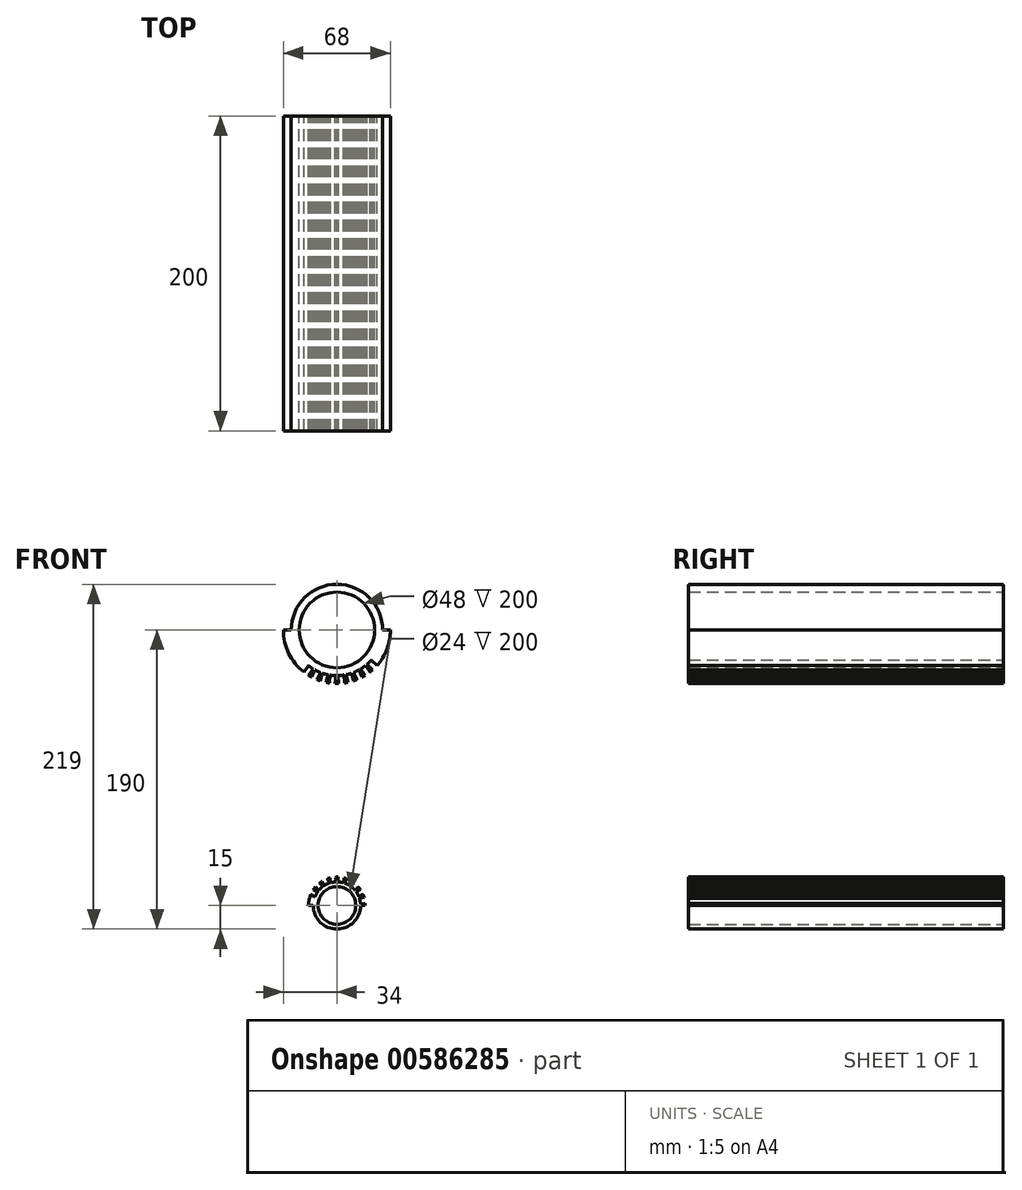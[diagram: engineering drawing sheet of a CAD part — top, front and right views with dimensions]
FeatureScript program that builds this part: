
annotation { "Feature Type Name" : "Feature", "Feature Type Description" : "" }
export const myFeature = defineFeature(function(context is Context, id is Id, definition is map)
    precondition{}
    {
        {
            var Q0;
            Q0=qCreatedBy(makeId("Front.planeOp"),FACE);
            cPlane(context, id + "F0", {"entities" : qUnion([Q0]), "cplaneType" : CPlaneType.OFFSET, "offset" : 100 * mm, "oppositeDirection" : true, "width" : 150 * mm, "height" : 150 * mm});
        }
        {
            var Q0;
            Q0=qCreatedBy(id+"F0.planeOp",FACE);
            var sketch = newSketch(context, id + "F1", { "sketchPlane" : qUnion([Q0])});
            skCircle(sketch, "E0", {"center": v(0, 0) * mm, "radius": 24 * mm});
            skArc(sketch, "E1", {"start": v(-18.13, -22.63) * mm, "mid": v(2.53, -28.89) * mm, "end": v(21.79, -19.14) * mm});
            skArc(sketch, "E2", {"start": v(-34, 0) * mm, "mid": v(-30.58, -14.86) * mm, "end": v(-21, -26.73) * mm});
            skLineSegment(sketch, "E3", {"start": v(-34, 0) * mm, "end": v(-29, 0) * mm});
            skLineSegment(sketch, "E4", {"start": v(29, 0) * mm, "end": v(34, 0) * mm});
            skLineSegment(sketch, "E5", {"start": v(-54.4, 0) * mm, "end": v(73.62, 0) * mm, "construction": true});
            skPoint(sketch, "E5.startSnap0", {"position": v(-31.5, 0) * mm});
            skLineSegment(sketch, "E6", {"start": v(0, 47.74) * mm, "end": v(0, -182.93) * mm, "construction": true});
            skLineSegment(sketch, "E7", {"start": v(0, 0) * mm, "end": v(2.1, -23.9) * mm, "construction": true});
            skLineSegment(sketch, "E8", {"start": v(2.1, -23.9) * mm, "end": v(2.53, -28.89) * mm, "construction": true});
            skLineSegment(sketch, "E9", {"start": v(2.53, -28.89) * mm, "end": v(3.01, -34.45) * mm});
            skLineSegment(sketch, "E10", {"start": v(4.83, -33.66) * mm, "end": v(4.4, -28.67) * mm});
            skLineSegment(sketch, "E11", {"start": v(1.1, -33.98) * mm, "end": v(0.65, -29) * mm});
            skLineSegment(sketch, "E12", {"start": v(0, 0) * mm, "end": v(6.21, -23.18) * mm, "construction": true});
            skLineSegment(sketch, "E13", {"start": v(7.5, -28.01) * mm, "end": v(8.74, -32.61) * mm});
            skLineSegment(sketch, "E14", {"start": v(6.21, -23.18) * mm, "end": v(7.5, -28.01) * mm, "construction": true});
            skLineSegment(sketch, "E15", {"start": v(5.68, -28.44) * mm, "end": v(6.98, -33.28) * mm});
            skLineSegment(sketch, "E16", {"start": v(9.3, -27.47) * mm, "end": v(10.6, -32.3) * mm});
            skLineSegment(sketch, "E17", {"start": v(0, 0) * mm, "end": v(10.14, -21.75) * mm, "construction": true});
            skLineSegment(sketch, "E18", {"start": v(12.65, -31.56) * mm, "end": v(10.53, -27.02) * mm});
            skLineSegment(sketch, "E19", {"start": v(13.93, -25.44) * mm, "end": v(16.05, -29.98) * mm});
            skLineSegment(sketch, "E20", {"start": v(12.26, -26.28) * mm, "end": v(14.23, -30.51) * mm});
            skLineSegment(sketch, "E21", {"start": v(10.14, -21.75) * mm, "end": v(12.26, -26.28) * mm, "construction": true});
            skLineSegment(sketch, "E22", {"start": v(0, 0) * mm, "end": v(13.77, -19.66) * mm, "construction": true});
            skLineSegment(sketch, "E23", {"start": v(18.13, -22.63) * mm, "end": v(21, -26.73) * mm});
            skLineSegment(sketch, "E24", {"start": v(15.06, -24.78) * mm, "end": v(17.94, -28.88) * mm});
            skLineSegment(sketch, "E25", {"start": v(16.63, -23.76) * mm, "end": v(19.52, -27.88) * mm});
            skLineSegment(sketch, "E26", {"start": v(13.77, -19.66) * mm, "end": v(16.63, -23.76) * mm, "construction": true});
            skLineSegment(sketch, "E27", {"start": v(0, 0) * mm, "end": v(16.97, -16.97) * mm, "construction": true});
            skLineSegment(sketch, "E28", {"start": v(25.33, -22.68) * mm, "end": v(21.79, -19.14) * mm});
            skLineSegment(sketch, "E29", {"start": v(19.14, -21.79) * mm, "end": v(22.68, -25.33) * mm});
            skLineSegment(sketch, "E30", {"start": v(20.5, -20.5) * mm, "end": v(26.16, -26.16) * mm});
            skLineSegment(sketch, "E31", {"start": v(16.97, -16.97) * mm, "end": v(20.5, -20.5) * mm, "construction": true});
            skLineSegment(sketch, "E32.MirrorCS", {"start": v(-1.1, -33.98) * mm, "end": v(-0.65, -29) * mm});
            skLineSegment(sketch, "E33.MirrorCS", {"start": v(-2.53, -28.89) * mm, "end": v(-3.05, -34.87) * mm});
            skLineSegment(sketch, "E34.MirrorCS", {"start": v(-4.83, -33.66) * mm, "end": v(-4.4, -28.67) * mm});
            skLineSegment(sketch, "E35.MirrorCS", {"start": v(-5.68, -28.44) * mm, "end": v(-6.98, -33.28) * mm});
            skLineSegment(sketch, "E36.MirrorCS", {"start": v(-7.5, -28.01) * mm, "end": v(-9.02, -33.65) * mm});
            skLineSegment(sketch, "E37.MirrorCS", {"start": v(-9.3, -27.47) * mm, "end": v(-10.6, -32.3) * mm});
            skLineSegment(sketch, "E38.MirrorCS", {"start": v(-12.65, -31.56) * mm, "end": v(-10.53, -27.02) * mm});
            skLineSegment(sketch, "E39.MirrorCS", {"start": v(-12.26, -26.28) * mm, "end": v(-14.94, -32.05) * mm});
            skLineSegment(sketch, "E40.MirrorCS", {"start": v(-13.93, -25.44) * mm, "end": v(-16.05, -29.98) * mm});
            skLineSegment(sketch, "E41.MirrorCS", {"start": v(-15.06, -24.78) * mm, "end": v(-17.94, -28.88) * mm});
            skLineSegment(sketch, "E42.MirrorCS", {"start": v(-16.63, -23.76) * mm, "end": v(-20.8, -29.7) * mm});
            skLineSegment(sketch, "E43.MirrorCS", {"start": v(-18.13, -22.63) * mm, "end": v(-21, -26.73) * mm});
            skLineSegment(sketch, "E44", {"start": v(0, 0) * mm, "end": v(20.78, -12) * mm, "construction": true});
            skLineSegment(sketch, "E45", {"start": v(25.11, -14.5) * mm, "end": v(32.04, -18.5) * mm, "construction": true});
            skLineSegment(sketch, "E46", {"start": v(20.78, -12) * mm, "end": v(25.11, -14.5) * mm, "construction": true});
            skLineSegment(sketch, "E47", {"start": v(26.16, -26.16) * mm, "end": v(32.04, -18.5) * mm});
            skLineSegment(sketch, "E48", {"start": v(32.04, -18.5) * mm, "end": v(169.42, -28.1) * mm});
            skCircle(sketch, "E49", {"center": v(0, -175) * mm, "radius": 12 * mm});
            skCircle(sketch, "E50", {"center": v(0, -175) * mm, "radius": 15 * mm});
            skArc(sketch, "E51", {"start": v(18, -175) * mm, "mid": v(17.99, -174.29) * mm, "end": v(17.94, -173.58) * mm});
            skLineSegment(sketch, "E52", {"start": v(-36.36, -175) * mm, "end": v(-18, -175) * mm, "construction": true});
            skLineSegment(sketch, "E53", {"start": v(18, -175) * mm, "end": v(43.93, -175) * mm, "construction": true});
            skLineSegment(sketch, "E54", {"start": v(-18, -175) * mm, "end": v(18, -175) * mm, "construction": true});
            skLineSegment(sketch, "E55", {"start": v(-18, -175) * mm, "end": v(-15, -175) * mm});
            skLineSegment(sketch, "E56", {"start": v(18, -175) * mm, "end": v(18, -175) * mm});
            skLineSegment(sketch, "E57", {"start": v(32.04, -18.5) * mm, "end": v(37.79, -18.5) * mm, "construction": true});
            skLineSegment(sketch, "E58", {"start": v(0, -175) * mm, "end": v(1.77, -163.13) * mm, "construction": true});
            skLineSegment(sketch, "E59", {"start": v(2.22, -160.16) * mm, "end": v(2.91, -155.51) * mm});
            skLineSegment(sketch, "E60", {"start": v(1.77, -163.13) * mm, "end": v(2.22, -160.16) * mm, "construction": true});
            skLineSegment(sketch, "E61", {"start": v(0.34, -160) * mm, "end": v(0.79, -157.02) * mm});
            skLineSegment(sketch, "E62", {"start": v(4.05, -160.56) * mm, "end": v(4.5, -157.57) * mm});
            skLineSegment(sketch, "E63", {"start": v(0, -175) * mm, "end": v(5.17, -164.17) * mm, "construction": true});
            skLineSegment(sketch, "E64", {"start": v(6.46, -161.46) * mm, "end": v(8.23, -157.75) * mm});
            skLineSegment(sketch, "E65", {"start": v(5.17, -164.17) * mm, "end": v(6.46, -161.46) * mm, "construction": true});
            skLineSegment(sketch, "E66", {"start": v(4.71, -160.76) * mm, "end": v(6.01, -158.03) * mm});
            skLineSegment(sketch, "E67", {"start": v(8.1, -162.37) * mm, "end": v(9.4, -159.65) * mm});
            skLineSegment(sketch, "E68", {"start": v(0, -175) * mm, "end": v(8.26, -166.3) * mm, "construction": true});
            skLineSegment(sketch, "E69", {"start": v(10.33, -164.12) * mm, "end": v(12.8, -161.5) * mm});
            skLineSegment(sketch, "E70", {"start": v(8.26, -166.3) * mm, "end": v(10.33, -164.12) * mm, "construction": true});
            skLineSegment(sketch, "E71", {"start": v(8.88, -162.91) * mm, "end": v(10.96, -160.72) * mm});
            skLineSegment(sketch, "E72", {"start": v(11.6, -165.5) * mm, "end": v(13.68, -163.3) * mm});
            skLineSegment(sketch, "E73", {"start": v(0, -175) * mm, "end": v(10.55, -169.27) * mm, "construction": true});
            skLineSegment(sketch, "E74", {"start": v(13.18, -167.84) * mm, "end": v(16.8, -165.88) * mm});
            skLineSegment(sketch, "E75", {"start": v(10.55, -169.27) * mm, "end": v(13.18, -167.84) * mm, "construction": true});
            skLineSegment(sketch, "E76", {"start": v(12.18, -166.25) * mm, "end": v(14.84, -164.8) * mm});
            skLineSegment(sketch, "E77", {"start": v(13.97, -169.54) * mm, "end": v(16.63, -168.1) * mm});
            skArc(sketch, "E78.trimOffspring", {"start": v(0.79, -157.02) * mm, "mid": v(0.4, -157) * mm, "end": v(0, -157) * mm});
            skArc(sketch, "E79.trimOffspring", {"start": v(6.01, -158.03) * mm, "mid": v(5.26, -157.79) * mm, "end": v(4.5, -157.57) * mm});
            skArc(sketch, "E80.trimOffspring", {"start": v(10.96, -160.72) * mm, "mid": v(10.2, -160.16) * mm, "end": v(9.4, -159.65) * mm});
            skArc(sketch, "E81.trimOffspring", {"start": v(14.84, -164.8) * mm, "mid": v(14.28, -164.04) * mm, "end": v(13.68, -163.3) * mm});
            skArc(sketch, "E82.trimOffspring", {"start": v(4.83, -33.66) * mm, "mid": v(5.9, -33.48) * mm, "end": v(6.98, -33.28) * mm});
            skArc(sketch, "E83.trimOffspring", {"start": v(10.6, -32.3) * mm, "mid": v(11.63, -31.95) * mm, "end": v(12.65, -31.56) * mm});
            skArc(sketch, "E84.trimOffspring", {"start": v(16.05, -29.98) * mm, "mid": v(17, -29.44) * mm, "end": v(17.94, -28.88) * mm});
            skArc(sketch, "E85.trimOffspring", {"start": v(21, -26.73) * mm, "mid": v(21.85, -26.05) * mm, "end": v(22.68, -25.33) * mm});
            skArc(sketch, "E86.trimOffspring", {"start": v(25.33, -22.68) * mm, "mid": v(31.76, -12.14) * mm, "end": v(34, 0) * mm});
            skArc(sketch, "E87.trimOffspring", {"start": v(-1.1, -33.98) * mm, "mid": v(0, -34) * mm, "end": v(1.1, -33.98) * mm});
            skArc(sketch, "E88.trimOffspring", {"start": v(-6.98, -33.28) * mm, "mid": v(-5.9, -33.48) * mm, "end": v(-4.83, -33.66) * mm});
            skArc(sketch, "E89.trimOffspring", {"start": v(-12.65, -31.56) * mm, "mid": v(-11.63, -31.95) * mm, "end": v(-10.6, -32.3) * mm});
            skArc(sketch, "E90.trimOffspring", {"start": v(-17.94, -28.88) * mm, "mid": v(-17, -29.44) * mm, "end": v(-16.05, -29.98) * mm});
            skLineSegment(sketch, "E91", {"start": v(0, -175) * mm, "end": v(11.8, -172.81) * mm, "construction": true});
            skLineSegment(sketch, "E92", {"start": v(14.75, -172.27) * mm, "end": v(30.22, -169.4) * mm});
            skLineSegment(sketch, "E93", {"start": v(11.8, -172.81) * mm, "end": v(14.75, -172.27) * mm, "construction": true});
            skLineSegment(sketch, "E94", {"start": v(14.3, -170.44) * mm, "end": v(17.26, -169.9) * mm});
            skLineSegment(sketch, "E95", {"start": v(14.97, -174.13) * mm, "end": v(17.94, -173.58) * mm});
            skLineSegment(sketch, "E96", {"start": v(18, -175) * mm, "end": v(15, -175) * mm});
            skArc(sketch, "E97.trimOffspring", {"start": v(17.26, -169.9) * mm, "mid": v(16.97, -168.99) * mm, "end": v(16.63, -168.1) * mm});
            skLineSegment(sketch, "E98.MirrorCS", {"start": v(-0.34, -160) * mm, "end": v(-0.79, -157.02) * mm});
            skLineSegment(sketch, "E99.MirrorCS", {"start": v(-2.22, -160.16) * mm, "end": v(-3, -154.93) * mm});
            skLineSegment(sketch, "E100.MirrorCS", {"start": v(-4.05, -160.56) * mm, "end": v(-4.5, -157.57) * mm});
            skLineSegment(sketch, "E101.MirrorCS", {"start": v(-4.71, -160.76) * mm, "end": v(-6.01, -158.03) * mm});
            skLineSegment(sketch, "E102.MirrorCS", {"start": v(-6.46, -161.46) * mm, "end": v(-9.01, -156.1) * mm});
            skLineSegment(sketch, "E103.MirrorCS", {"start": v(-8.1, -162.37) * mm, "end": v(-9.4, -159.65) * mm});
            skLineSegment(sketch, "E104.MirrorCS", {"start": v(-8.88, -162.91) * mm, "end": v(-10.96, -160.72) * mm});
            skLineSegment(sketch, "E105.MirrorCS", {"start": v(-10.33, -164.12) * mm, "end": v(-15, -159.2) * mm});
            skLineSegment(sketch, "E106.MirrorCS", {"start": v(-11.6, -165.5) * mm, "end": v(-13.68, -163.3) * mm});
            skLineSegment(sketch, "E107.MirrorCS", {"start": v(-12.18, -166.25) * mm, "end": v(-14.84, -164.8) * mm});
            skLineSegment(sketch, "E108.MirrorCS", {"start": v(-13.18, -167.84) * mm, "end": v(-20.89, -163.66) * mm});
            skLineSegment(sketch, "E109.MirrorCS", {"start": v(-13.97, -169.54) * mm, "end": v(-16.63, -168.1) * mm});
            skArc(sketch, "E110.trimOffspring", {"start": v(-4.5, -157.57) * mm, "mid": v(-5.26, -157.79) * mm, "end": v(-6.01, -158.03) * mm});
            skArc(sketch, "E111.trimOffspring", {"start": v(-9.4, -159.65) * mm, "mid": v(-10.2, -160.16) * mm, "end": v(-10.96, -160.72) * mm});
            skArc(sketch, "E112.trimOffspring", {"start": v(-13.68, -163.3) * mm, "mid": v(-14.28, -164.04) * mm, "end": v(-14.84, -164.8) * mm});
            skArc(sketch, "E113.trimOffspring", {"start": v(-16.63, -168.1) * mm, "mid": v(-17.65, -171.48) * mm, "end": v(-18, -175) * mm});
            skArc(sketch, "E114.trimOffspring", {"start": v(29, 0) * mm, "mid": v(0, 29) * mm, "end": v(-29, 0) * mm});
            skArc(sketch, "E115.MirrorCS", {"start": v(-0.79, -157.02) * mm, "mid": v(-0.4, -157) * mm, "end": v(0, -157) * mm});
            skLineSegment(sketch, "E116", {"start": v(3, -37.93) * mm, "end": v(3, -151.93) * mm});
            skLineSegment(sketch, "E117", {"start": v(9, -36.68) * mm, "end": v(9, -153.09) * mm});
            skLineSegment(sketch, "E118", {"start": v(3.04, -35.28) * mm, "end": v(3, -37.8) * mm});
            skPoint(sketch, "E119.visualSharp", {"position": v(3.05, -34.87) * mm});
            skArc(sketch, "E119.filletArc", {"start": v(3.04, -35.28) * mm, "mid": v(3.04, -34.87) * mm, "end": v(3.01, -34.45) * mm});
            skPoint(sketch, "E120.visualSharp", {"position": v(3, -37.87) * mm});
            skArc(sketch, "E120.filletArc", {"start": v(3, -37.8) * mm, "mid": v(3, -37.87) * mm, "end": v(3, -37.93) * mm});
            skLineSegment(sketch, "E121", {"start": v(3, -151.93) * mm, "end": v(3, -154.33) * mm});
            skPoint(sketch, "E122.visualSharp", {"position": v(3, -154.93) * mm});
            skArc(sketch, "E122.filletArc", {"start": v(2.91, -155.51) * mm, "mid": v(2.98, -154.92) * mm, "end": v(3, -154.33) * mm});
            skLineSegment(sketch, "E123", {"start": v(9.01, -34.73) * mm, "end": v(9, -36.63) * mm});
            skPoint(sketch, "E124.visualSharp", {"position": v(9.02, -33.65) * mm});
            skArc(sketch, "E124.filletArc", {"start": v(9.01, -34.73) * mm, "mid": v(8.95, -33.66) * mm, "end": v(8.74, -32.61) * mm});
            skPoint(sketch, "E125.visualSharp", {"position": v(9, -36.65) * mm});
            skArc(sketch, "E125.filletArc", {"start": v(9, -36.63) * mm, "mid": v(9, -36.65) * mm, "end": v(9, -36.68) * mm});
            skLineSegment(sketch, "E126", {"start": v(9, -153.12) * mm, "end": v(9, -154.27) * mm});
            skPoint(sketch, "E127.visualSharp", {"position": v(9.01, -156.1) * mm});
            skArc(sketch, "E127.filletArc", {"start": v(8.23, -157.75) * mm, "mid": v(8.81, -156.06) * mm, "end": v(9, -154.27) * mm});
            skPoint(sketch, "E128.visualSharp", {"position": v(9, -153.1) * mm});
            skArc(sketch, "E128.filletArc", {"start": v(9, -153.09) * mm, "mid": v(9, -153.1) * mm, "end": v(9, -153.12) * mm});
            skLineSegment(sketch, "E129", {"start": v(15, -35.05) * mm, "end": v(15, -156) * mm});
            skLineSegment(sketch, "E130", {"start": v(14.98, -33.75) * mm, "end": v(15, -35.05) * mm});
            skPoint(sketch, "E131.visualSharp", {"position": v(14.94, -32.05) * mm});
            skArc(sketch, "E131.filletArc", {"start": v(14.98, -33.75) * mm, "mid": v(14.77, -32.09) * mm, "end": v(14.23, -30.51) * mm});
            skPoint(sketch, "E132.visualSharp", {"position": v(15, -159.2) * mm});
            skArc(sketch, "E132.filletArc", {"start": v(12.8, -161.5) * mm, "mid": v(14.43, -158.97) * mm, "end": v(15, -156) * mm});
            skLineSegment(sketch, "E133", {"start": v(21, -32.7) * mm, "end": v(21, -157.66) * mm});
            skLineSegment(sketch, "E134", {"start": v(20.95, -31.94) * mm, "end": v(21, -32.7) * mm});
            skPoint(sketch, "E135.visualSharp", {"position": v(20.8, -29.7) * mm});
            skArc(sketch, "E135.filletArc", {"start": v(20.95, -31.94) * mm, "mid": v(20.51, -29.8) * mm, "end": v(19.52, -27.88) * mm});
            skLineSegment(sketch, "E136", {"start": v(21, -157.66) * mm, "end": v(20.98, -159) * mm});
            skPoint(sketch, "E137.visualSharp", {"position": v(20.89, -163.66) * mm});
            skArc(sketch, "E137.filletArc", {"start": v(16.8, -165.88) * mm, "mid": v(19.81, -163) * mm, "end": v(20.98, -159) * mm});
            skSolve(sketch);
        }
        {
            var Q0;
            Q0=makeQuery(id+"F1.imprint","IMPRINT",FACE,{"disambiguationData":[TD([[makeQuery(id+"F1.imprint","IMPRINT",EDGE,{"derivedFrom":sQuery(id+"F1.wireOp",EDGE,"E0")}),-1.0]])]});
            var Q1;
            {var subQ0=sQuery(id+"F1.wireOp",EDGE,"E40.MirrorCS");Q1=makeQuery(id+"F1.imprint","IMPRINT",FACE,{"disambiguationData":[TD([[makeQuery(id+"F1.imprint","IMPRINT",EDGE,{"derivedFrom":subQ0}),-1.0]])]});}
            var Q2;
            {var subQ0=sQuery(id+"F1.wireOp",EDGE,"E37.MirrorCS");Q2=makeQuery(id+"F1.imprint","IMPRINT",FACE,{"disambiguationData":[TD([[makeQuery(id+"F1.imprint","IMPRINT",EDGE,{"derivedFrom":subQ0}),-1.0]])]});}
            var Q3;
            {var subQ0=sQuery(id+"F1.wireOp",EDGE,"E34.MirrorCS");Q3=makeQuery(id+"F1.imprint","IMPRINT",FACE,{"disambiguationData":[TD([[makeQuery(id+"F1.imprint","IMPRINT",EDGE,{"derivedFrom":subQ0}),1.0]])]});}
            var Q4;
            {var subQ0=sQuery(id+"F1.wireOp",EDGE,"E11");Q4=makeQuery(id+"F1.imprint","IMPRINT",FACE,{"disambiguationData":[TD([[makeQuery(id+"F1.imprint","IMPRINT",EDGE,{"derivedFrom":subQ0}),1.0]])]});}
            var Q5;
            {var subQ0=sQuery(id+"F1.wireOp",EDGE,"E10");Q5=makeQuery(id+"F1.imprint","IMPRINT",FACE,{"disambiguationData":[TD([[makeQuery(id+"F1.imprint","IMPRINT",EDGE,{"derivedFrom":subQ0}),-1.0]])]});}
            var Q6;
            {var subQ0=sQuery(id+"F1.wireOp",EDGE,"E16");Q6=makeQuery(id+"F1.imprint","IMPRINT",FACE,{"disambiguationData":[TD([[makeQuery(id+"F1.imprint","IMPRINT",EDGE,{"derivedFrom":subQ0}),1.0]])]});}
            var Q7;
            {var subQ0=sQuery(id+"F1.wireOp",EDGE,"E19");Q7=makeQuery(id+"F1.imprint","IMPRINT",FACE,{"disambiguationData":[TD([[makeQuery(id+"F1.imprint","IMPRINT",EDGE,{"derivedFrom":subQ0}),1.0]])]});}
            var Q8;
            {var subQ0=sQuery(id+"F1.wireOp",EDGE,"E23");Q8=makeQuery(id+"F1.imprint","IMPRINT",FACE,{"disambiguationData":[TD([[makeQuery(id+"F1.imprint","IMPRINT",EDGE,{"derivedFrom":subQ0}),1.0]])]});}
            var Q9;
            {var subQ0=sQuery(id+"F1.wireOp",EDGE,"E55");Q9=makeQuery(id+"F1.imprint","IMPRINT",FACE,{"disambiguationData":[TD([[makeQuery(id+"F1.imprint","IMPRINT",EDGE,{"derivedFrom":subQ0}),1.0]])]});}
            var Q10;
            {var subQ0=sQuery(id+"F1.wireOp",EDGE,"E106.MirrorCS");Q10=makeQuery(id+"F1.imprint","IMPRINT",FACE,{"disambiguationData":[TD([[makeQuery(id+"F1.imprint","IMPRINT",EDGE,{"derivedFrom":subQ0}),1.0]])]});}
            var Q11;
            {var subQ0=sQuery(id+"F1.wireOp",EDGE,"E103.MirrorCS");Q11=makeQuery(id+"F1.imprint","IMPRINT",FACE,{"disambiguationData":[TD([[makeQuery(id+"F1.imprint","IMPRINT",EDGE,{"derivedFrom":subQ0}),1.0]])]});}
            var Q12;
            Q12=makeQuery(id+"F1.imprint","IMPRINT",FACE,{"disambiguationData":[TD([[makeQuery(id+"F1.imprint","IMPRINT",EDGE,{"derivedFrom":sQuery(id+"F1.wireOp",EDGE,"E49")}),-1.0]])]});
            var Q13;
            {var subQ0=sQuery(id+"F1.wireOp",EDGE,"E100.MirrorCS");Q13=makeQuery(id+"F1.imprint","IMPRINT",FACE,{"disambiguationData":[TD([[makeQuery(id+"F1.imprint","IMPRINT",EDGE,{"derivedFrom":subQ0}),1.0]])]});}
            var Q14;
            {var subQ1=sQuery(id+"F1.wireOp",EDGE,"E61");Q14=makeQuery(id+"F1.imprint","IMPRINT",FACE,{"disambiguationData":[TD([[makeQuery(id+"F1.imprint","IMPRINT",EDGE,{"derivedFrom":subQ1}),1.0]])]});}
            var Q15;
            {var subQ0=sQuery(id+"F1.wireOp",EDGE,"E62");Q15=makeQuery(id+"F1.imprint","IMPRINT",FACE,{"disambiguationData":[TD([[makeQuery(id+"F1.imprint","IMPRINT",EDGE,{"derivedFrom":subQ0}),-1.0]])]});}
            var Q16;
            {var subQ0=sQuery(id+"F1.wireOp",EDGE,"E67");Q16=makeQuery(id+"F1.imprint","IMPRINT",FACE,{"disambiguationData":[TD([[makeQuery(id+"F1.imprint","IMPRINT",EDGE,{"derivedFrom":subQ0}),-1.0]])]});}
            var Q17;
            {var subQ0=sQuery(id+"F1.wireOp",EDGE,"E72");Q17=makeQuery(id+"F1.imprint","IMPRINT",FACE,{"disambiguationData":[TD([[makeQuery(id+"F1.imprint","IMPRINT",EDGE,{"derivedFrom":subQ0}),-1.0]])]});}
            var Q18;
            {var subQ0=sQuery(id+"F1.wireOp",EDGE,"E77");Q18=makeQuery(id+"F1.imprint","IMPRINT",FACE,{"disambiguationData":[TD([[makeQuery(id+"F1.imprint","IMPRINT",EDGE,{"derivedFrom":subQ0}),-1.0]])]});}
            var Q19;
            Q19=makeQuery(id+"F1.imprint","IMPRINT",FACE,{"disambiguationData":[TD([[makeQuery(id+"F1.imprint","IMPRINT",EDGE,{"derivedFrom":sQuery(id+"F1.wireOp",EDGE,"E51")}),1.0]])]});
            extrude(context, id + "F2", {"entities" : qUnion([Q0, Q1, Q2, Q3, Q4, Q5, Q6, Q7, Q8, Q9, Q10, Q11, Q12, Q13, Q14, Q15, Q16, Q17, Q18, Q19]), "endBound" : BoundingType.SYMMETRIC, "depth" : 200 * mm, "offsetDistance" : 25 * mm});
        }
    });
